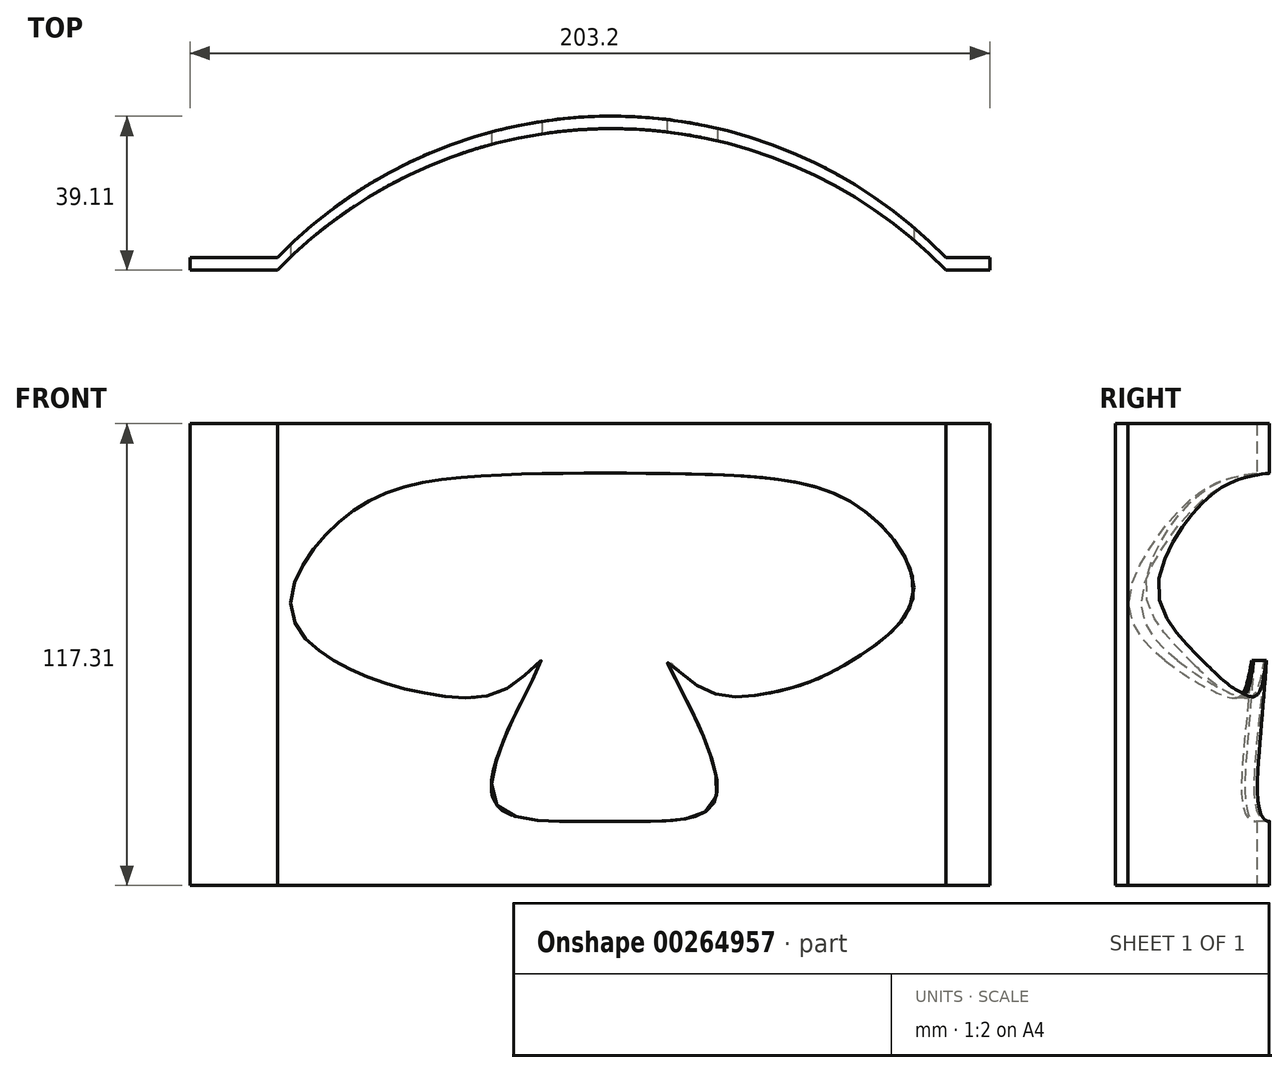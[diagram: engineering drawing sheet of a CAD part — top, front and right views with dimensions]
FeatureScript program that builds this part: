
annotation { "Feature Type Name" : "Feature", "Feature Type Description" : "" }
export const myFeature = defineFeature(function(context is Context, id is Id, definition is map)
    precondition{}
    {
        {
            var Q0;
            Q0=qCreatedBy(makeId("Top.planeOp"),FACE);
            var sketch = newSketch(context, id + "F0", { "sketchPlane" : qUnion([Q0])});
            skLineSegment(sketch, "E0.MirrorCS", {"start": v(-105.33, -9.73) * mm, "end": v(-83.1, -9.73) * mm});
            skLineSegment(sketch, "E1.MirrorCS", {"start": v(97.87, -9.73) * mm, "end": v(86.76, -9.73) * mm});
            skPoint(sketch, "E2.MirrorP", {"position": v(101.05, -9.73) * mm});
            skArc(sketch, "E3.MirrorCS", {"start": v(-83.1, -9.73) * mm, "mid": v(1.83, 26.21) * mm, "end": v(86.76, -9.73) * mm});
            skPoint(sketch, "E4.MirrorP", {"position": v(-108.5, -9.73) * mm});
            skPoint(sketch, "E5.MirrorP", {"position": v(1.79, -9.47) * mm});
            skLineSegment(sketch, "E6.MirrorCS", {"start": v(-105.33, -12.9) * mm, "end": v(-83.1, -12.9) * mm});
            skLineSegment(sketch, "E7.MirrorCS", {"start": v(97.87, -12.9) * mm, "end": v(86.76, -12.9) * mm});
            skPoint(sketch, "E8.MirrorP", {"position": v(101.05, -20.9) * mm});
            skArc(sketch, "E9.MirrorCS", {"start": v(-83.1, -12.9) * mm, "mid": v(1.83, 23.04) * mm, "end": v(86.76, -12.9) * mm});
            skPoint(sketch, "E10.MirrorP", {"position": v(-108.5, -20.9) * mm});
            skPoint(sketch, "E11.MirrorP", {"position": v(1.79, -20.65) * mm});
            skLineSegment(sketch, "E12", {"start": v(-105.33, -9.73) * mm, "end": v(-105.33, -12.9) * mm});
            skLineSegment(sketch, "E13", {"start": v(97.87, -9.73) * mm, "end": v(97.87, -12.9) * mm});
            skSolve(sketch);
        }
        {
            var Q0;
            Q0=makeQuery(id+"F0.imprint","IMPRINT",FACE,{"disambiguationData":[TD([[makeQuery(id+"F0.imprint","IMPRINT",EDGE,{"derivedFrom":sQuery(id+"F0.wireOp",EDGE,"E0.MirrorCS")}),-1.0]])]});
            extrude(context, id + "F1", {"entities" : qUnion([Q0]), "depth" : 117.3 * mm, "offsetDistance" : 25.4 * mm});
        }
        {
            var Q0;
            Q0=qCreatedBy(makeId("Front.planeOp"),FACE);
            cPlane(context, id + "F2", {"entities" : qUnion([Q0]), "cplaneType" : CPlaneType.OFFSET, "offset" : 31.5 * mm, "width" : 152.4 * mm, "height" : 152.4 * mm});
        }
        {
            var Q0;
            Q0=qCreatedBy(id+"F2.planeOp",FACE);
            var sketch = newSketch(context, id + "F3", { "sketchPlane" : qUnion([Q0])});
            skLineSegment(sketch, "E14.MirrorCS", {"start": v(-93.95, 119.73) * mm, "end": v(-95.54, 119.73) * mm});
            skLineSegment(sketch, "E15.MirrorCS", {"start": v(-93.95, 0.83) * mm, "end": v(-95.54, 0.83) * mm});
            skLineSegment(sketch, "E16.MirrorCS", {"start": v(-106.44, 119.73) * mm, "end": v(-108.02, 119.73) * mm});
            skLineSegment(sketch, "E17.MirrorCS", {"start": v(-108.02, 0.83) * mm, "end": v(-106.44, 0.83) * mm});
            skLineSegment(sketch, "E18.MirrorCS", {"start": v(-95.54, 119.73) * mm, "end": v(-106.44, 119.73) * mm});
            skLineSegment(sketch, "E19.MirrorCS", {"start": v(-106.44, 0.83) * mm, "end": v(-95.54, 0.83) * mm});
            skLineSegment(sketch, "E20.MirrorCS", {"start": v(-10.68, 0.72) * mm, "end": v(-10.68, 0.83) * mm});
            skLineSegment(sketch, "E21.MirrorCS", {"start": v(113.85, 119.73) * mm, "end": v(92.06, 119.73) * mm});
            skPoint(sketch, "E22.MirrorP", {"position": v(-95.54, 121.35) * mm});
            skLineSegment(sketch, "E23.MirrorCS", {"start": v(4.9, 119.73) * mm, "end": v(-93.95, 119.73) * mm});
            skFitSpline(sketch, "E24.MirrorCS", {"points": [v(-68.76, 57.16) * mm, v(-79.6, 73.36) * mm, v(-64.54, 94.66) * mm, v(0.1, 104.73) * mm], "startDerivative": vector(-98.96, 57.83) * mm, "endDerivative": vector(254.08, 0.52) * mm});
            skFitSpline(sketch, "E25.MirrorCS", {"points": [v(-68.76, 57.16) * mm, v(-43.24, 48.4) * mm, v(-23.97, 50.49) * mm, v(-15.88, 57.03) * mm, v(-28.68, 24) * mm, v(-0.02, 16.28) * mm], "startDerivative": vector(117.08, -69.28) * mm, "endDerivative": vector(198.32, -0.54) * mm});
            skLineSegment(sketch, "E26.MirrorCS", {"start": v(92.86, 119.73) * mm, "end": v(4.9, 119.73) * mm});
            skLineSegment(sketch, "E27.MirrorCS", {"start": v(92.86, 0.83) * mm, "end": v(4.9, 0.83) * mm});
            skPoint(sketch, "E28.MirrorP", {"position": v(-106.44, 0.83) * mm});
            skLineSegment(sketch, "E29.MirrorCS", {"start": v(-108.02, 119.73) * mm, "end": v(-108.02, 0.83) * mm});
            skPoint(sketch, "E30.MirrorP", {"position": v(-92.43, 42.57) * mm});
            skPoint(sketch, "E31.MirrorP", {"position": v(92.06, 23.75) * mm});
            skPoint(sketch, "E32.MirrorP", {"position": v(-95.54, 49.26) * mm});
            skLineSegment(sketch, "E33.MirrorCS", {"start": v(-93.95, 0.83) * mm, "end": v(4.9, 0.83) * mm});
            skLineSegment(sketch, "E34.MirrorCS", {"start": v(-95.54, 119.73) * mm, "end": v(-95.54, 0.83) * mm});
            skLineSegment(sketch, "E35.MirrorCS", {"start": v(113.85, 0.83) * mm, "end": v(92.06, 0.83) * mm});
            skPoint(sketch, "E36.MirrorP", {"position": v(-95.54, 119.73) * mm});
            skLineSegment(sketch, "E37.MirrorCS", {"start": v(92.86, 119.73) * mm, "end": v(92.86, 0.83) * mm});
            skLineSegment(sketch, "E38.MirrorCS", {"start": v(113.85, 119.73) * mm, "end": v(113.85, 0.83) * mm});
            skFitSpline(sketch, "E39.MirrorCS", {"points": [v(60.9, 55.93) * mm, v(78.55, 74.22) * mm, v(65.86, 95.3) * mm, v(0.1, 104.73) * mm], "startDerivative": vector(99.1, 57.58) * mm, "endDerivative": vector(-254.08, 1.16) * mm});
            skFitSpline(sketch, "E40.MirrorCS", {"points": [v(60.9, 55.93) * mm, v(40.47, 48.61) * mm, v(24.02, 50.43) * mm, v(15.95, 57) * mm, v(28.66, 23.93) * mm, v(-0.02, 16.28) * mm], "startDerivative": vector(-117.26, -69) * mm, "endDerivative": vector(-198.32, -0.05) * mm});
            skSolve(sketch);
        }
        {
            var Q0;
            Q0=makeQuery(id+"F3.imprint","IMPRINT",FACE,{"disambiguationData":[TD([[makeQuery(id+"F3.imprint","IMPRINT",EDGE,{"derivedFrom":sQuery(id+"F3.wireOp",EDGE,"E24.MirrorCS")}),-1.0]])]});
            extrude(context, id + "F4", {"entities" : qUnion([Q0]), "operationType" : NewBodyOperationType.REMOVE, "oppositeDirection" : true, "depth" : 86.1 * mm, "offsetDistance" : 25.4 * mm});
        }
    });
